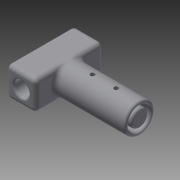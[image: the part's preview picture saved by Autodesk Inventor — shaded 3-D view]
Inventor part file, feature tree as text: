
AUTODESK INVENTOR PART (.ipt)
format: ipt  version: 2014 (Build 180170000, 170)  size: 586,752 bytes
history: native  units: mm
features: fillet x7, sketch x6, extrude x5, emboss x1, plane x1
ambient origin geometry x8: Origin, YZ Plane, XZ Plane, XY Plane, X Axis, Y Axis, Z Axis, Center Point
bodies: Solid1 (feature_tree)
feature tree (20):
  extrude  "Extrusion1"  Depth=50.8mm
  extrude  "Extrusion2"  Depth=25.4mm
  extrude  "Extrusion3"  Depth=34.0868mm
  fillet  "Fillet3"  Radius=25.3238mm
  fillet  "Fillet4"  Radius=99.06mm
  fillet  "Fillet6"  Radius=22.0472mm
  emboss  "Emboss1"
  extrude  "Extrusion5"  Depth=6.35mm
  fillet  "Fillet9"  Radius=6.35mm
  fillet  "Fillet10"  Radius=6.35mm
  fillet  "Fillet14"  Radius=13.0mm
  fillet  "Fillet15"  Radius=2.0mm
  plane  "Work Plane1"
  extrude  "Extrusion6"  Depth=6.35mm
  sketch  "Sketch1"  dims[d0=149.86mm d1=50.8mm]
  sketch  "Sketch2"  dims[d2=44.45mm d3=25.4mm]
  sketch  "Sketch3"  dims[d4=44.45mm d5=0.0mm d6=34.0868mm d7=25.3238mm d8=99.06mm d9=0.0mm d10=22.0472mm]
  sketch  "Sketch5"  dims[d11=152.4mm d12=0.0mm d15=6.35mm d16=6.35mm d18=6.35mm d25=13.0mm d26=2.0mm d27=0.0mm]
  sketch  "Sketch6"  dims[d29=105.41mm d30=0.0mm d31=6.35mm]
  sketch  "Sketch9"  dims[d32=6.35mm d36=3.175mm d37=3.175mm d38=44.45mm d39=6.604mm d40=44.45mm d41=0.0mm d42=35.56mm d43=71.12mm]
